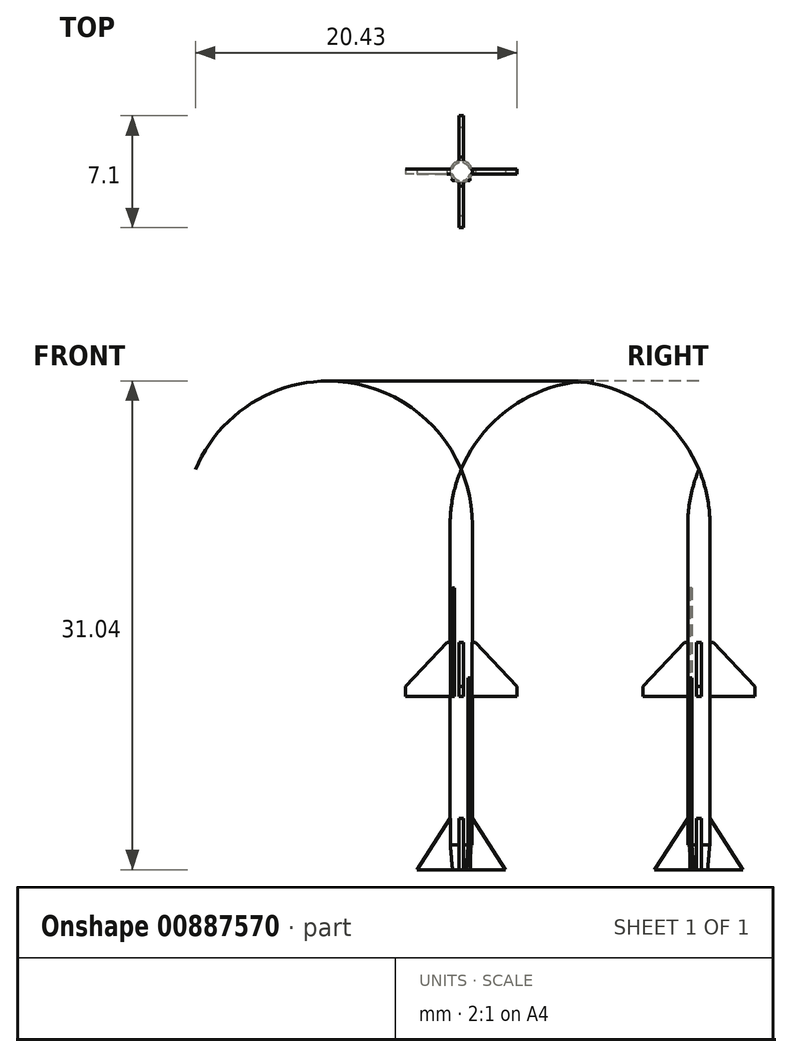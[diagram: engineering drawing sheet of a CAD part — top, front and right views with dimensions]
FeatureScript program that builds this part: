
annotation { "Feature Type Name" : "Feature", "Feature Type Description" : "" }
export const myFeature = defineFeature(function(context is Context, id is Id, definition is map)
    precondition{}
    {
        {
            var Q0;
            Q0=qCreatedBy(makeId("Front.planeOp"),FACE);
            var sketch = newSketch(context, id + "F0", { "sketchPlane" : qUnion([Q0])});
            skLineSegment(sketch, "E0", {"start": v(0, 0) * mm, "end": v(0, 25.42) * mm});
            skLineSegment(sketch, "E1", {"start": v(0.7, 21.9) * mm, "end": v(0.7, 0) * mm});
            skLineSegment(sketch, "E2", {"start": v(0.7, 0) * mm, "end": v(0, 0) * mm});
            skArc(sketch, "E3", {"start": v(0.7, 21.9) * mm, "mid": v(0.53, 23.7) * mm, "end": v(0, 25.42) * mm});
            skSolve(sketch);
        }
        {
            var Q0;
            Q0=makeQuery(id+"F0.imprint","IMPRINT",FACE,{"disambiguationData":[TD([[makeQuery(id+"F0.imprint","IMPRINT",EDGE,{"derivedFrom":sQuery(id+"F0.wireOp",EDGE,"E0")}),-1.0]])]});
            var Q1;
            Q1=sQuery(id+"F0.wireOp",EDGE,"E0");
            revolve(context, id + "F1", {"surfaceOperationType" : NewSurfaceOperationType.NEW, "entities" : qUnion([Q0]), "axis" : qUnion([Q1]), "revolveType" : RevolveType.FULL});
        }
        {
            var Q0;
            Q0=qCreatedBy(makeId("Front.planeOp"),FACE);
            var sketch = newSketch(context, id + "F2", { "sketchPlane" : qUnion([Q0])});
            skLineSegment(sketch, "E4", {"start": v(0.57, 0) * mm, "end": v(0.7, 1.56) * mm});
            skLineSegment(sketch, "E5", {"start": v(0.7, 1.56) * mm, "end": v(1.57, 1.56) * mm});
            skLineSegment(sketch, "E6", {"start": v(1.57, 1.56) * mm, "end": v(1.57, 0) * mm});
            skLineSegment(sketch, "E7", {"start": v(1.57, 0) * mm, "end": v(0.57, 0) * mm});
            skLineSegment(sketch, "E8.0", {"start": v(0.7, 0) * mm, "end": v(-0.7, 0) * mm});
            skSolve(sketch);
        }
        {
            var Q0;
            Q0=qSketchRegion(id+"F2",true);
            var Q1;
            Q1=makeQuery(id+"F1.opRevolve","SWEPT_FACE",FACE,{"disambiguationData":[OSD([sQuery(id+"F0.wireOp",EDGE,"E1")])]});
            revolve(context, id + "F3", {"operationType" : NewBodyOperationType.REMOVE, "surfaceOperationType" : NewSurfaceOperationType.NEW, "entities" : qUnion([Q0]), "axis" : qUnion([Q1]), "revolveType" : RevolveType.FULL, "oppositeDirection" : true});
        }
        {
            var Q0;
            Q0=qCreatedBy(makeId("Front.planeOp"),FACE);
            var sketch = newSketch(context, id + "F4", { "sketchPlane" : qUnion([Q0])});
            skLineSegment(sketch, "E9", {"start": v(-0.7, 14.44) * mm, "end": v(0.7, 14.44) * mm});
            skLineSegment(sketch, "E10", {"start": v(3.55, 11.02) * mm, "end": v(0.7, 11.02) * mm});
            skLineSegment(sketch, "E11", {"start": v(0.7, 3.26) * mm, "end": v(2.81, 0) * mm});
            skLineSegment(sketch, "E12", {"start": v(2.81, 0) * mm, "end": v(-2.81, 0) * mm});
            skLineSegment(sketch, "E13", {"start": v(-2.81, 0) * mm, "end": v(-0.7, 3.26) * mm});
            skLineSegment(sketch, "E14", {"start": v(-0.7, 11.02) * mm, "end": v(-3.55, 11.02) * mm});
            skLineSegment(sketch, "E15.0", {"start": v(0.7, 21.9) * mm, "end": v(-0.7, 21.9) * mm});
            skLineSegment(sketch, "E16.top", {"start": v(-0.17, 0) * mm, "end": v(0.17, 0) * mm});
            skLineSegment(sketch, "E17", {"start": v(-3.55, 11.65) * mm, "end": v(-3.55, 11.02) * mm});
            skLineSegment(sketch, "E18", {"start": v(3.55, 11.02) * mm, "end": v(3.55, 11.65) * mm});
            skLineSegment(sketch, "E19", {"start": v(-0.7, 14.44) * mm, "end": v(-0.91, 14.44) * mm});
            skLineSegment(sketch, "E20", {"start": v(-0.91, 14.44) * mm, "end": v(-3.55, 11.65) * mm});
            skLineSegment(sketch, "E21", {"start": v(0.7, 14.44) * mm, "end": v(0.91, 14.44) * mm});
            skLineSegment(sketch, "E22", {"start": v(0.91, 14.44) * mm, "end": v(3.55, 11.65) * mm});
            skLineSegment(sketch, "E23", {"start": v(-0.7, 3.26) * mm, "end": v(0.7, 3.26) * mm});
            skLineSegment(sketch, "E24", {"start": v(-0.7, 11.02) * mm, "end": v(0.7, 11.02) * mm});
            skSolve(sketch);
        }
        {
            var Q0;
            Q0=makeQuery(id+"F4.imprint","IMPRINT",FACE,{"disambiguationData":[TD([[makeQuery(id+"F4.imprint","IMPRINT",EDGE,{"derivedFrom":sQuery(id+"F4.wireOp",EDGE,"E9")}),-1.0]])]});
            var Q1;
            {var subQ3=sQuery(id+"F4.wireOp",EDGE,"E11");Q1=makeQuery(id+"F4.imprint","IMPRINT",FACE,{"disambiguationData":[TD([[makeQuery(id+"F4.imprint","IMPRINT",EDGE,{"derivedFrom":subQ3}),-1.0]])]});}
            extrude(context, id + "F5", {"entities" : qUnion([Q0, Q1]), "operationType" : NewBodyOperationType.ADD, "oppositeDirection" : true, "depth" : 0.3 * mm, "offsetDistance" : 25 * mm, "symmetric" : true});
        }
        {
            var Q0;
            Q0=makeQuery(id+"F1.opRevolve","SWEPT_BODY",BODY,{"disambiguationData":[OSD([sQuery(id+"F0.wireOp",EDGE,"E0"),sQuery(id+"F0.wireOp",EDGE,"E1"),sQuery(id+"F0.wireOp",EDGE,"E2"),sQuery(id+"F0.wireOp",EDGE,"E3")])]});
            var Q1;
            Q1=makeQuery(id+"F1.opRevolve","SWEPT_FACE",FACE,{"disambiguationData":[OSD([sQuery(id+"F0.wireOp",EDGE,"E1")])]});
            circularPattern(context, id + "F6", {"operationType" : NewBodyOperationType.ADD, "entities" : qUnion([Q0]), "axis" : qUnion([Q1]), "angle" : 360 * degree, "instanceCount" : 4, "equalSpace" : true, "computeTransformsWithoutBuiltin" : true});
        }
        {
            var Q0;
            {var subQ2=sQuery(id+"F4.wireOp",EDGE,"E21");var subQ3=sQuery(id+"F4.wireOp",EDGE,"E20");var subQ4=sQuery(id+"F4.wireOp",EDGE,"E19");var subQ9=sQuery(id+"F4.wireOp",EDGE,"E9");Q0=makeQuery(id+"F5.boolean.opBoolean","SPLIT",FACE,{"disambiguationData":[TD([makeQuery(id+"F5.opExtrude","SWEPT_FACE",FACE,{"disambiguationData":[OSD([subQ3])]})])],"derivedFrom":makeQuery(id+"F5.opExtrude","SWEPT_FACE",FACE,{"disambiguationData":[OSD([subQ9,subQ4,subQ2])]})});}
            var sketch = newSketch(context, id + "F7", { "sketchPlane" : qUnion([Q0])});
            skCircle(sketch, "E25.1", {"center": v(0, 0) * mm, "radius": 0.7 * mm});
            skLineSegment(sketch, "E26.0.0", {"start": v(0, 0) * mm, "end": v(-0.51, 0) * mm, "construction": true});
            skLineSegment(sketch, "E27", {"start": v(-0.32, -0.44) * mm, "end": v(-0.44, -0.32) * mm});
            skLineSegment(sketch, "E28", {"start": v(-0.44, -0.32) * mm, "end": v(-0.55, -0.44) * mm});
            skLineSegment(sketch, "E29", {"start": v(-0.44, -0.55) * mm, "end": v(-0.32, -0.44) * mm});
            skLineSegment(sketch, "E30", {"start": v(0, 0) * mm, "end": v(-0.38, -0.38) * mm, "construction": true});
            skArc(sketch, "E31", {"start": v(-0.55, -0.44) * mm, "mid": v(-0.56, -0.56) * mm, "end": v(-0.44, -0.55) * mm});
            skSolve(sketch);
        }
        {
            var Q0;
            {var subQ0=sQuery(id+"F7.wireOp",EDGE,"E31");Q0=makeQuery(id+"F7.imprint","IMPRINT",FACE,{"disambiguationData":[TD([[makeQuery(id+"F7.imprint","IMPRINT",EDGE,{"derivedFrom":subQ0}),1.0]])]});}
            var Q1;
            {var subQ1=sQuery(id+"F7.wireOp",EDGE,"E28");Q1=makeQuery(id+"F7.imprint","IMPRINT",FACE,{"disambiguationData":[TD([[makeQuery(id+"F7.imprint","IMPRINT",EDGE,{"derivedFrom":subQ1}),1.0]])]});}
            extrude(context, id + "F8", {"entities" : qUnion([Q0, Q1]), "operationType" : NewBodyOperationType.ADD, "depth" : (965 / 144) * mm, "offsetDistance" : 25 * mm, "symmetric" : true});
        }
        {
            var Q0;
            Q0=makeQuery(id+"F1.opRevolve","SWEPT_FACE",FACE,{"disambiguationData":[OSD([sQuery(id+"F0.wireOp",EDGE,"E2")])]});
            var sketch = newSketch(context, id + "F9", { "sketchPlane" : qUnion([Q0])});
            skLineSegment(sketch, "E32", {"start": v(0, 0) * mm, "end": v(0, 0) * mm});
            skLineSegment(sketch, "E33", {"start": v(0, 0) * mm, "end": v(0.44, 0) * mm, "construction": true});
            skCircle(sketch, "E34.0.0", {"center": v(0, 0) * mm, "radius": 0.57 * mm});
            skLineSegment(sketch, "E35", {"start": v(0.44, 0.55) * mm, "end": v(0.34, 0.46) * mm});
            skLineSegment(sketch, "E36", {"start": v(0.34, 0.46) * mm, "end": v(0.46, 0.34) * mm});
            skLineSegment(sketch, "E37", {"start": v(0.46, 0.34) * mm, "end": v(0.55, 0.44) * mm});
            skLineSegment(sketch, "E38", {"start": v(0, 0) * mm, "end": v(0.4, 0.4) * mm, "construction": true});
            skCircle(sketch, "E39.0", {"center": v(0, 0) * mm, "radius": 0.7 * mm});
            skArc(sketch, "E40", {"start": v(0.55, 0.44) * mm, "mid": v(0.55, 0.55) * mm, "end": v(0.44, 0.55) * mm});
            skLineSegment(sketch, "E41", {"start": v(0.44, 0.55) * mm, "end": v(0.55, 0.44) * mm, "construction": true});
            skSolve(sketch);
        }
        {
            var Q0;
            {var subQ0=sQuery(id+"F9.wireOp",EDGE,"E40");Q0=makeQuery(id+"F9.imprint","IMPRINT",FACE,{"disambiguationData":[TD([[makeQuery(id+"F9.imprint","IMPRINT",EDGE,{"derivedFrom":subQ0}),1.0]])]});}
            var Q1;
            {var subQ1=sQuery(id+"F9.wireOp",EDGE,"E35");Q1=makeQuery(id+"F9.imprint","IMPRINT",FACE,{"disambiguationData":[TD([[makeQuery(id+"F9.imprint","IMPRINT",EDGE,{"derivedFrom":subQ1}),1.0]])]});}
            extrude(context, id + "F10", {"entities" : qUnion([Q0, Q1]), "operationType" : NewBodyOperationType.ADD, "oppositeDirection" : true, "depth" : (1740 / 144) * mm, "offsetDistance" : 25 * mm});
        }
        {
            var Q0;
            Q0=makeQuery(id+"F8.boolean.opBoolean","INTERSECT",EDGE,{"derivedFrom":[makeQuery(id+"F1SgjpEdBBOFuZJ_3.boolean.opBoolean","SPLIT",FACE,{"disambiguationData":[TD([makeQuery(id+"F1SgjpEdBBOFuZJ_3.opRevolve","SWEPT_FACE",FACE,{"disambiguationData":[OSD([sQuery(id+"FlY5MtBrKRYJxzp_3.wireOp",EDGE,"kaf6A2uF-OX8H-Va1Y-guTc-rQCtsMHh0R69")])]})])],"derivedFrom":makeQuery(id+"F1.opRevolve","SWEPT_FACE",FACE,{"disambiguationData":[OSD([sQuery(id+"F0.wireOp",EDGE,"E1")])]})}),makeQuery(id+"F8.opExtrude","CAP_FACE",FACE,{"disambiguationData":[OSD([sQuery(id+"F7.wireOp",EDGE,"E26.0.2"),sQuery(id+"F7.wireOp",EDGE,"E28"),sQuery(id+"F7.wireOp",EDGE,"E29"),sQuery(id+"F7.wireOp",EDGE,"E31")])],"isStart":false})]});
            var Q1;
            Q1=makeQuery(id+"F8.boolean.opBoolean","INTERSECT",EDGE,{"derivedFrom":[makeQuery(id+"F1SgjpEdBBOFuZJ_3.boolean.opBoolean","SPLIT",FACE,{"disambiguationData":[TD([makeQuery(id+"F1SgjpEdBBOFuZJ_3.opRevolve","SWEPT_FACE",FACE,{"disambiguationData":[OSD([sQuery(id+"FlY5MtBrKRYJxzp_3.wireOp",EDGE,"HS1JStHF-Ansh-H00f-Jenc-fMZRPMrZ2prO")])]})])],"derivedFrom":makeQuery(id+"F1.opRevolve","SWEPT_FACE",FACE,{"disambiguationData":[OSD([sQuery(id+"F0.wireOp",EDGE,"E1")])]})}),makeQuery(id+"F8.opExtrude","CAP_FACE",FACE,{"disambiguationData":[OSD([sQuery(id+"F7.wireOp",EDGE,"E26.0.2"),sQuery(id+"F7.wireOp",EDGE,"E28"),sQuery(id+"F7.wireOp",EDGE,"E29"),sQuery(id+"F7.wireOp",EDGE,"E31")])],"isStart":true})]});
            var Q2;
            Q2=makeQuery(id+"F10.boolean.opBoolean","INTERSECT",EDGE,{"derivedFrom":[makeQuery(id+"F1SgjpEdBBOFuZJ_3.boolean.opBoolean","SPLIT",FACE,{"disambiguationData":[TD([makeQuery(id+"F1SgjpEdBBOFuZJ_3.opRevolve","SWEPT_FACE",FACE,{"disambiguationData":[OSD([sQuery(id+"FlY5MtBrKRYJxzp_3.wireOp",EDGE,"kaf6A2uF-OX8H-Va1Y-guTc-rQCtsMHh0R69")])]})])],"derivedFrom":makeQuery(id+"F1.opRevolve","SWEPT_FACE",FACE,{"disambiguationData":[OSD([sQuery(id+"F0.wireOp",EDGE,"E1")])]})}),makeQuery(id+"F10.opExtrude","CAP_FACE",FACE,{"disambiguationData":[OSD([sQuery(id+"F9.wireOp",EDGE,"E34.0.0"),sQuery(id+"F9.wireOp",EDGE,"E35"),sQuery(id+"F9.wireOp",EDGE,"E37"),sQuery(id+"F9.wireOp",EDGE,"E40")])],"isStart":false})]});
            chamfer(context, id + "F11", {"entities" : qUnion([Q0, Q1, Q2]), "width" : .1 * mm, "tangentPropagation" : true});
        }
    });
